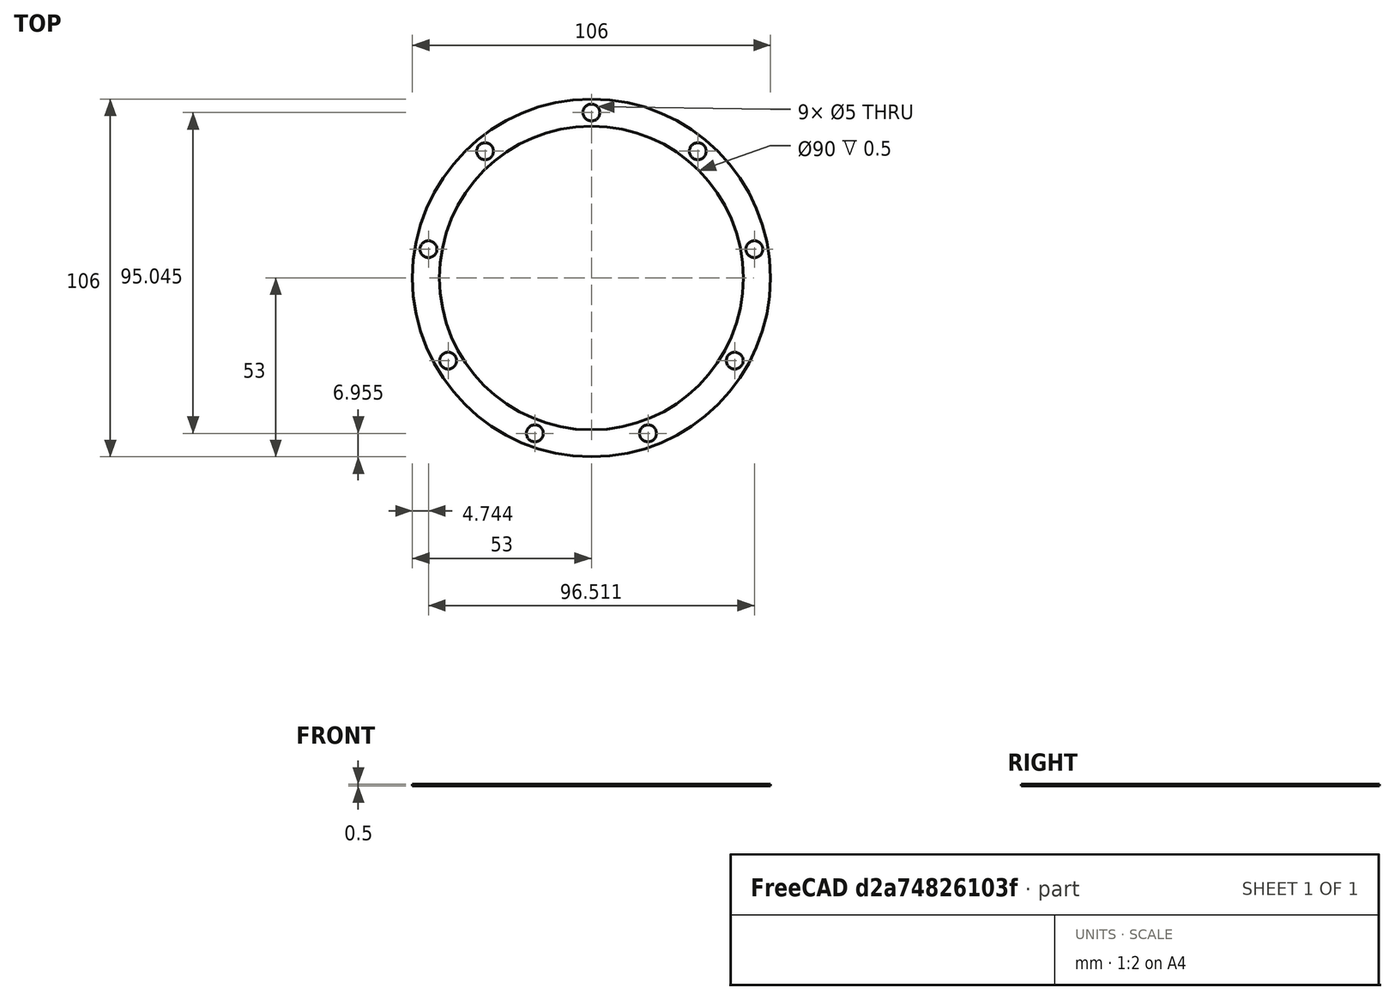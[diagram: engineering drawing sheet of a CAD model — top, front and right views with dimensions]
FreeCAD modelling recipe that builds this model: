
FCSTD DOCUMENT  (FreeCAD 0.19R24276 (Git))
Label: BLDC_GT2_part_1_d75_d128_v2_for_disk_bolgarki_temp
License: All rights reserved
LicenseURL: http://en.wikipedia.org/wiki/All_rights_reserved
objects: Sketcher::SketchObject×1, PartDesign::Pad×1, PartDesign::Body×1
note: 4 computed .brp shape members not serialized (recipe doc carries the construction recipe); baked Part::Feature solids carry a one-line shape summary decoded from their .brp

FEATURE [Sketcher::SketchObject] Sketch  label="Sketch_d67_d113x6otvxd4.2_d128"
  FullyConstrained = true
  MapMode = 5
  Support = -> [XY_Plane]
  sketch-geometry (21):
    g0: Circle CenterX=0 CenterY=1e-16 CenterZ=0 NormalX=0 NormalY=0 NormalZ=1 AngleXU=0 Radius=53
    g1: Circle CenterX=0 CenterY=1e-16 CenterZ=0 NormalX=0 NormalY=0 NormalZ=1 AngleXU=0 Radius=45
    g2: LineSegment StartX=0 StartY=49 StartZ=0 EndX=-31.4966 EndY=37.5362 EndZ=0
    g3: LineSegment StartX=-31.4966 StartY=37.5362 StartZ=0 EndX=-48.2556 EndY=8.50876 EndZ=0
    g4: LineSegment StartX=-48.2556 StartY=8.50876 StartZ=0 EndX=-42.4352 EndY=-24.5 EndZ=0
    g5: LineSegment StartX=-42.4352 StartY=-24.5 StartZ=0 EndX=-16.759 EndY=-46.0449 EndZ=0
    g6: LineSegment StartX=-16.759 StartY=-46.0449 StartZ=0 EndX=16.759 EndY=-46.0449 EndZ=0
    g7: LineSegment StartX=16.759 StartY=-46.0449 StartZ=0 EndX=42.4352 EndY=-24.5 EndZ=0
    g8: LineSegment StartX=42.4352 StartY=-24.5 StartZ=0 EndX=48.2556 EndY=8.50876 EndZ=0
    g9: LineSegment StartX=48.2556 StartY=8.50876 StartZ=0 EndX=31.4966 EndY=37.5362 EndZ=0
    g10: LineSegment StartX=31.4966 StartY=37.5362 StartZ=0 EndX=0 EndY=49 EndZ=0
    g11: Circle CenterX=0 CenterY=1e-16 CenterZ=0 NormalX=0 NormalY=0 NormalZ=1 AngleXU=0 Radius=49
    g12: Circle CenterX=31.4966 CenterY=37.5362 CenterZ=0 NormalX=0 NormalY=0 NormalZ=1 AngleXU=0 Radius=2.5
    g13: Circle CenterX=48.2556 CenterY=8.50876 CenterZ=0 NormalX=0 NormalY=0 NormalZ=1 AngleXU=0 Radius=2.5
    g14: Circle CenterX=42.4352 CenterY=-24.5 CenterZ=0 NormalX=0 NormalY=0 NormalZ=1 AngleXU=0 Radius=2.5
    g15: Circle CenterX=16.759 CenterY=-46.0449 CenterZ=0 NormalX=0 NormalY=0 NormalZ=1 AngleXU=0 Radius=2.5
    g16: Circle CenterX=-16.759 CenterY=-46.0449 CenterZ=0 NormalX=0 NormalY=0 NormalZ=1 AngleXU=0 Radius=2.5
    g17: Circle CenterX=-42.4352 CenterY=-24.5 CenterZ=0 NormalX=0 NormalY=0 NormalZ=1 AngleXU=0 Radius=2.5
    g18: Circle CenterX=-48.2556 CenterY=8.50876 CenterZ=0 NormalX=0 NormalY=0 NormalZ=1 AngleXU=0 Radius=2.5
    g19: Circle CenterX=-31.4966 CenterY=37.5362 CenterZ=0 NormalX=0 NormalY=0 NormalZ=1 AngleXU=0 Radius=2.5
    g20: Circle CenterX=0 CenterY=49 CenterZ=0 NormalX=0 NormalY=0 NormalZ=1 AngleXU=0 Radius=2.5
  constraints (37):
    c: Coincident(g0,g-1)
    c: Diameter(g0) = 106
    c: Coincident(g1,g0)
    c: Diameter(g1) = 90
    c: Coincident(g2,g3)
    c: Coincident(g3,g4)
    c: Coincident(g4,g5)
    c: Coincident(g5,g6)
    c: Coincident(g6,g7)
    c: Coincident(g7,g8)
    c: Coincident(g8,g9)
    c: Coincident(g9,g10)
    c: Coincident(g10,g2)
    c: Equal(g2, g3-g10) x8
    c: PointOnObject(g2,g11)
    c: PointOnObject(g3,g11)
    c: PointOnObject(g4,g11)
    c: PointOnObject(g5,g11)
    c: PointOnObject(g6,g11)
    c: PointOnObject(g7,g11)
    c: PointOnObject(g8,g11)
    c: PointOnObject(g9,g11)
    c: PointOnObject(g10,g11)
    c: Coincident(g11,g0)
    c: Diameter(g11) = 98
    c: Coincident(g12,g9)
    c: Coincident(g13,g8)
    c: Coincident(g14,g7)
    c: Coincident(g15,g6)
    c: Coincident(g16,g5)
    c: Coincident(g17,g4)
    c: Coincident(g18,g3)
    c: Coincident(g19,g2)
    c: Coincident(g20,g2)
    c: Vertical(g20,g0)
    c: Diameter(g20) = 5
    c: Equal(g20, g12-g19) x8
FEATURE [PartDesign::Pad] Pad  label="Pad_h3"
  Direction = (1,1,1)
  Length = 0.5
  Length2 = 100
  Profile = -> Sketch
  Type = 0
FEATURE [PartDesign::Body] Body
  Group = -> [Sketch,Pad]
  Origin = -> Origin
  Tip = -> Pad
